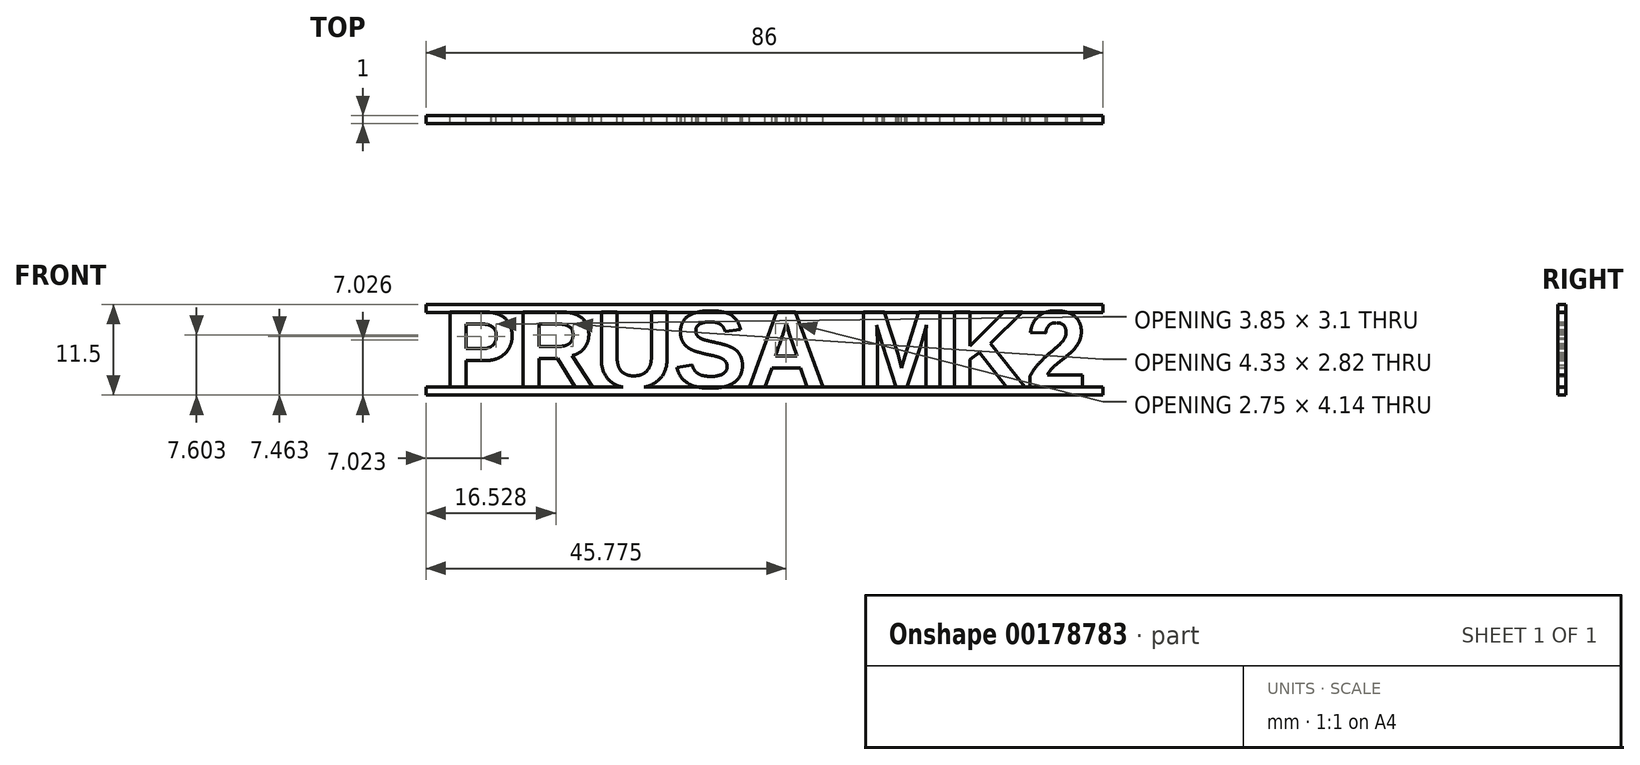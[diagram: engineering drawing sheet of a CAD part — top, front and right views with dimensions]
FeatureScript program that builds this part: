
annotation { "Feature Type Name" : "Feature", "Feature Type Description" : "" }
export const myFeature = defineFeature(function(context is Context, id is Id, definition is map)
    precondition{}
    {
        {
            var Q0;
            Q0=qCreatedBy(makeId("Front.planeOp"),FACE);
            var sketch = newSketch(context, id + "F0", { "sketchPlane" : qUnion([Q0])});
            skText(sketch, "E0", { "text": "PRUSA MK2", "fontName": "Arimo-Bold.ttf"});
            skLineSegment(sketch, "E1.bottom", {"start": v(-40.27, 10) * mm, "end": v(45.73, 10) * mm});
            skLineSegment(sketch, "E1.top", {"start": v(-40.27, 11) * mm, "end": v(45.73, 11) * mm});
            skLineSegment(sketch, "E1.left", {"start": v(-40.27, 10) * mm, "end": v(-40.27, 11) * mm});
            skLineSegment(sketch, "E1.right", {"start": v(45.73, 10) * mm, "end": v(45.73, 11) * mm});
            skLineSegment(sketch, "E2.0", {"start": v(-40.27, 15.74) * mm, "end": v(45.73, 15.74) * mm, "construction": true});
            skLineSegment(sketch, "E3.MirrorCS", {"start": v(-40.27, 20.5) * mm, "end": v(45.73, 20.5) * mm});
            skLineSegment(sketch, "E4.MirrorCS", {"start": v(-40.27, 21.5) * mm, "end": v(-40.27, 20.5) * mm});
            skLineSegment(sketch, "E5.MirrorCS", {"start": v(-40.27, 21.5) * mm, "end": v(45.73, 21.5) * mm});
            skLineSegment(sketch, "E6.MirrorCS", {"start": v(45.73, 21.5) * mm, "end": v(45.73, 20.5) * mm});
            skLineSegment(sketch, "E7.left", {"start": v(-40.27, 21.5) * mm, "end": v(-40.27, 10) * mm});
            skLineSegment(sketch, "E7.right", {"start": v(45.73, 21.5) * mm, "end": v(45.73, 10) * mm});
            const initialGuessF0  = {"E0": [-0.0381, 0.011, 1, 0, 0.01]};
            skSetInitialGuess(sketch, initialGuessF0);
            skSolve(sketch);
        }
        {
            var Q0;
            Q0=makeQuery(id+"F0.imprint","IMPRINT",FACE,{"disambiguationData":[TD([[makeQuery(id+"F0.imprint","IMPRINT",EDGE,{"derivedFrom":sQuery(id+"F0.wireOp",EDGE,"E0.sketch_text.stroke-0")}),-1.0]])]});
            var Q1;
            Q1=makeQuery(id+"F0.imprint","IMPRINT",FACE,{"disambiguationData":[TD([[makeQuery(id+"F0.imprint","IMPRINT",EDGE,{"derivedFrom":sQuery(id+"F0.wireOp",EDGE,"E0.sketch_text.stroke-16")}),-1.0]])]});
            var Q2;
            Q2=makeQuery(id+"F0.imprint","IMPRINT",FACE,{"disambiguationData":[TD([[makeQuery(id+"F0.imprint","IMPRINT",EDGE,{"derivedFrom":sQuery(id+"F0.wireOp",EDGE,"E0.sketch_text.stroke-34")}),-1.0]])]});
            var Q3;
            Q3=makeQuery(id+"F0.imprint","IMPRINT",FACE,{"disambiguationData":[TD([[makeQuery(id+"F0.imprint","IMPRINT",EDGE,{"derivedFrom":sQuery(id+"F0.wireOp",EDGE,"E0.sketch_text.stroke-48")}),-1.0]])]});
            var Q4;
            Q4=makeQuery(id+"F0.imprint","IMPRINT",FACE,{"disambiguationData":[TD([[makeQuery(id+"F0.imprint","IMPRINT",EDGE,{"derivedFrom":sQuery(id+"F0.wireOp",EDGE,"E0.sketch_text.stroke-79")}),-1.0]])]});
            var Q5;
            Q5=makeQuery(id+"F0.imprint","IMPRINT",FACE,{"disambiguationData":[TD([[makeQuery(id+"F0.imprint","IMPRINT",EDGE,{"derivedFrom":sQuery(id+"F0.wireOp",EDGE,"E0.sketch_text.stroke-94")}),-1.0]])]});
            var Q6;
            Q6=makeQuery(id+"F0.imprint","IMPRINT",FACE,{"disambiguationData":[TD([[makeQuery(id+"F0.imprint","IMPRINT",EDGE,{"derivedFrom":sQuery(id+"F0.wireOp",EDGE,"E0.sketch_text.stroke-115")}),-1.0]])]});
            var Q7;
            Q7=makeQuery(id+"F0.imprint","IMPRINT",FACE,{"disambiguationData":[TD([[makeQuery(id+"F0.imprint","IMPRINT",EDGE,{"derivedFrom":sQuery(id+"F0.wireOp",EDGE,"E0.sketch_text.stroke-127")}),-1.0]])]});
            var Q8;
            Q8=makeQuery(id+"F0.imprint","IMPRINT",FACE,{"disambiguationData":[TD([[makeQuery(id+"F0.imprint","IMPRINT",EDGE,{"derivedFrom":sQuery(id+"F0.wireOp",EDGE,"E1.bottom")}),1.0]])]});
            var Q9;
            {var subQ0=sQuery(id+"F0.wireOp",EDGE,"E0.sketch_text.stroke-35");Q9=makeQuery(id+"F0.imprint","IMPRINT",FACE,{"disambiguationData":[TD([[makeQuery(id+"F0.imprint","IMPRINT",EDGE,{"derivedFrom":subQ0}),-1.0]])]});}
            var Q10;
            {var subQ39=sQuery(id+"F0.wireOp",EDGE,"E0.sketch_text.stroke-7");Q10=makeQuery(id+"F0.imprint","IMPRINT",FACE,{"disambiguationData":[TD([[makeQuery(id+"F0.imprint","IMPRINT",EDGE,{"derivedFrom":subQ39}),1.0]])]});}
            var Q11;
            {var subQ19=sQuery(id+"F0.wireOp",EDGE,"E1.bottom");Q11=makeQuery(id+"F0.imprint","IMPRINT",FACE,{"disambiguationData":[TD([[makeQuery(id+"F0.imprint","IMPRINT",EDGE,{"derivedFrom":subQ19}),1.0]])]});}
            extrude(context, id + "F1", {"entities" : qUnion([Q0, Q1, Q2, Q3, Q4, Q5, Q6, Q7, Q8, Q9, Q10, Q11]), "depth" : 1 * mm});
        }
        {
            var Q0;
            {var subQ0=sQuery(id+"F0.wireOp",EDGE,"E0.sketch_text.stroke-7");Q0=makeQuery(id+"F0.imprint","IMPRINT",FACE,{"disambiguationData":[TD([[makeQuery(id+"F0.imprint","IMPRINT",EDGE,{"derivedFrom":subQ0}),-1.0]])]});}
            var Q1;
            {var subQ0=sQuery(id+"F0.wireOp",EDGE,"E0.sketch_text.stroke-21");Q1=makeQuery(id+"F0.imprint","IMPRINT",FACE,{"disambiguationData":[TD([[makeQuery(id+"F0.imprint","IMPRINT",EDGE,{"derivedFrom":subQ0}),-1.0]])]});}
            var Q2;
            {var subQ0=sQuery(id+"F0.wireOp",EDGE,"E0.sketch_text.stroke-37");Q2=makeQuery(id+"F0.imprint","IMPRINT",FACE,{"disambiguationData":[TD([[makeQuery(id+"F0.imprint","IMPRINT",EDGE,{"derivedFrom":subQ0}),-1.0]])]});}
            var Q3;
            {var subQ0=sQuery(id+"F0.wireOp",EDGE,"E0.sketch_text.stroke-44");Q3=makeQuery(id+"F0.imprint","IMPRINT",FACE,{"disambiguationData":[TD([[makeQuery(id+"F0.imprint","IMPRINT",EDGE,{"derivedFrom":subQ0}),-1.0]])]});}
            var Q4;
            {var subQ0=sQuery(id+"F0.wireOp",EDGE,"E0.sketch_text.stroke-66");var subQ1=sQuery(id+"F0.wireOp",EDGE,"E0.sketch_text.stroke-65");var subQ2=makeQuery(id+"F0.imprint","INTERSECT",VERTEX,{"derivedFrom":[subQ1,subQ0]});Q4=makeQuery(id+"F0.imprint","IMPRINT",FACE,{"disambiguationData":[TD([[makeQuery(id+"F0.imprint","IMPRINT",EDGE,{"disambiguationData":[TD([[subQ2,1.0]])],"derivedFrom":subQ1}),-1.0]])]});}
            var Q5;
            {var subQ0=sQuery(id+"F0.wireOp",EDGE,"E0.sketch_text.stroke-84");Q5=makeQuery(id+"F0.imprint","IMPRINT",FACE,{"disambiguationData":[TD([[makeQuery(id+"F0.imprint","IMPRINT",EDGE,{"derivedFrom":subQ0}),-1.0]])]});}
            var Q6;
            {var subQ0=sQuery(id+"F0.wireOp",EDGE,"E0.sketch_text.stroke-106");Q6=makeQuery(id+"F0.imprint","IMPRINT",FACE,{"disambiguationData":[TD([[makeQuery(id+"F0.imprint","IMPRINT",EDGE,{"derivedFrom":subQ0}),-1.0]])]});}
            var Q7;
            {var subQ0=sQuery(id+"F0.wireOp",EDGE,"E0.sketch_text.stroke-112");Q7=makeQuery(id+"F0.imprint","IMPRINT",FACE,{"disambiguationData":[TD([[makeQuery(id+"F0.imprint","IMPRINT",EDGE,{"derivedFrom":subQ0}),-1.0]])]});}
            var Q8;
            {var subQ0=sQuery(id+"F0.wireOp",EDGE,"E0.sketch_text.stroke-120");Q8=makeQuery(id+"F0.imprint","IMPRINT",FACE,{"disambiguationData":[TD([[makeQuery(id+"F0.imprint","IMPRINT",EDGE,{"derivedFrom":subQ0}),-1.0]])]});}
            var Q9;
            {var subQ0=sQuery(id+"F0.wireOp",EDGE,"E0.sketch_text.stroke-123");Q9=makeQuery(id+"F0.imprint","IMPRINT",FACE,{"disambiguationData":[TD([[makeQuery(id+"F0.imprint","IMPRINT",EDGE,{"derivedFrom":subQ0}),-1.0]])]});}
            var Q10;
            {var subQ0=sQuery(id+"F0.wireOp",EDGE,"E0.sketch_text.stroke-138");var subQ1=sQuery(id+"F0.wireOp",EDGE,"E0.sketch_text.stroke-137");var subQ2=makeQuery(id+"F0.imprint","INTERSECT",VERTEX,{"derivedFrom":[subQ1,subQ0]});Q10=makeQuery(id+"F0.imprint","IMPRINT",FACE,{"disambiguationData":[TD([[makeQuery(id+"F0.imprint","IMPRINT",EDGE,{"disambiguationData":[TD([[subQ2,1.0]])],"derivedFrom":subQ1}),-1.0]])]});}
            var Q11;
            {var subQ0=sQuery(id+"F0.wireOp",EDGE,"E0.sketch_text.stroke-50");var subQ1=sQuery(id+"F0.wireOp",EDGE,"E0.sketch_text.stroke-49");var subQ2=makeQuery(id+"F0.imprint","INTERSECT",VERTEX,{"derivedFrom":[subQ1,subQ0]});Q11=makeQuery(id+"F0.imprint","IMPRINT",FACE,{"disambiguationData":[TD([[makeQuery(id+"F0.imprint","IMPRINT",EDGE,{"disambiguationData":[TD([[subQ2,1.0]])],"derivedFrom":subQ1}),-1.0]])]});}
            extrude(context, id + "F2", {"entities" : qUnion([Q0, Q1, Q2, Q3, Q4, Q5, Q6, Q7, Q8, Q9, Q10, Q11]), "depth" : 1 * mm});
        }
    });
